# Revit family: Paper Dispenser_Metlam_Vertical_Rounded
name_source: partatom
category: Specialty Equipment
revit_build: Autodesk Revit 2016 (Build: 20170117_1200(x64)
units: mm (PartAtom-declared; Revit-internal decimal feet)

## family parameters
Always vertical = Yes
Cut with Voids When Loaded = No
OmniClass Number = 23.40.20.21.17
OmniClass Title = Paper Towel Dispensers, Disposal Units
Part Type = Normal
Room Calculation Point = Yes
Round Connector Dimension = Use Diameter
Shared = No
Work Plane-Based = No

## types (1)
- 280w x 125d x 348h (ML725L_AR)
    Description = Ellipse Paper Towel Dispenser
    Manufacturer = Metlam
    Manufacturer_Overall Depth = 125 mm  [stored 0.410105 ft]
    Manufacturer_Overall Height = 348 mm  [stored 1.14173 ft]
    Manufacturer_Overall Width = 280 mm  [stored 0.918635 ft]
    Manufacturer_Spec Code = ML725L_AR
    Manufacturer_URL__Product Specific = https://www.metlam.com.au
    Material_ANZRS = z_Metlam_Metal_Stainless Steel_Satin
    Model = ML725L_AR
    Type Comments = Paper Towel Dispensers
    URL = http://www.metlam.com.au

note: [stored X ft] marks values corroborated as IEEE doubles in the binary element streams (Revit-internal decimal feet)

## geometry (parser evidence)
native form markers: Sweep x2
no freeform markers — native parametric forms only
